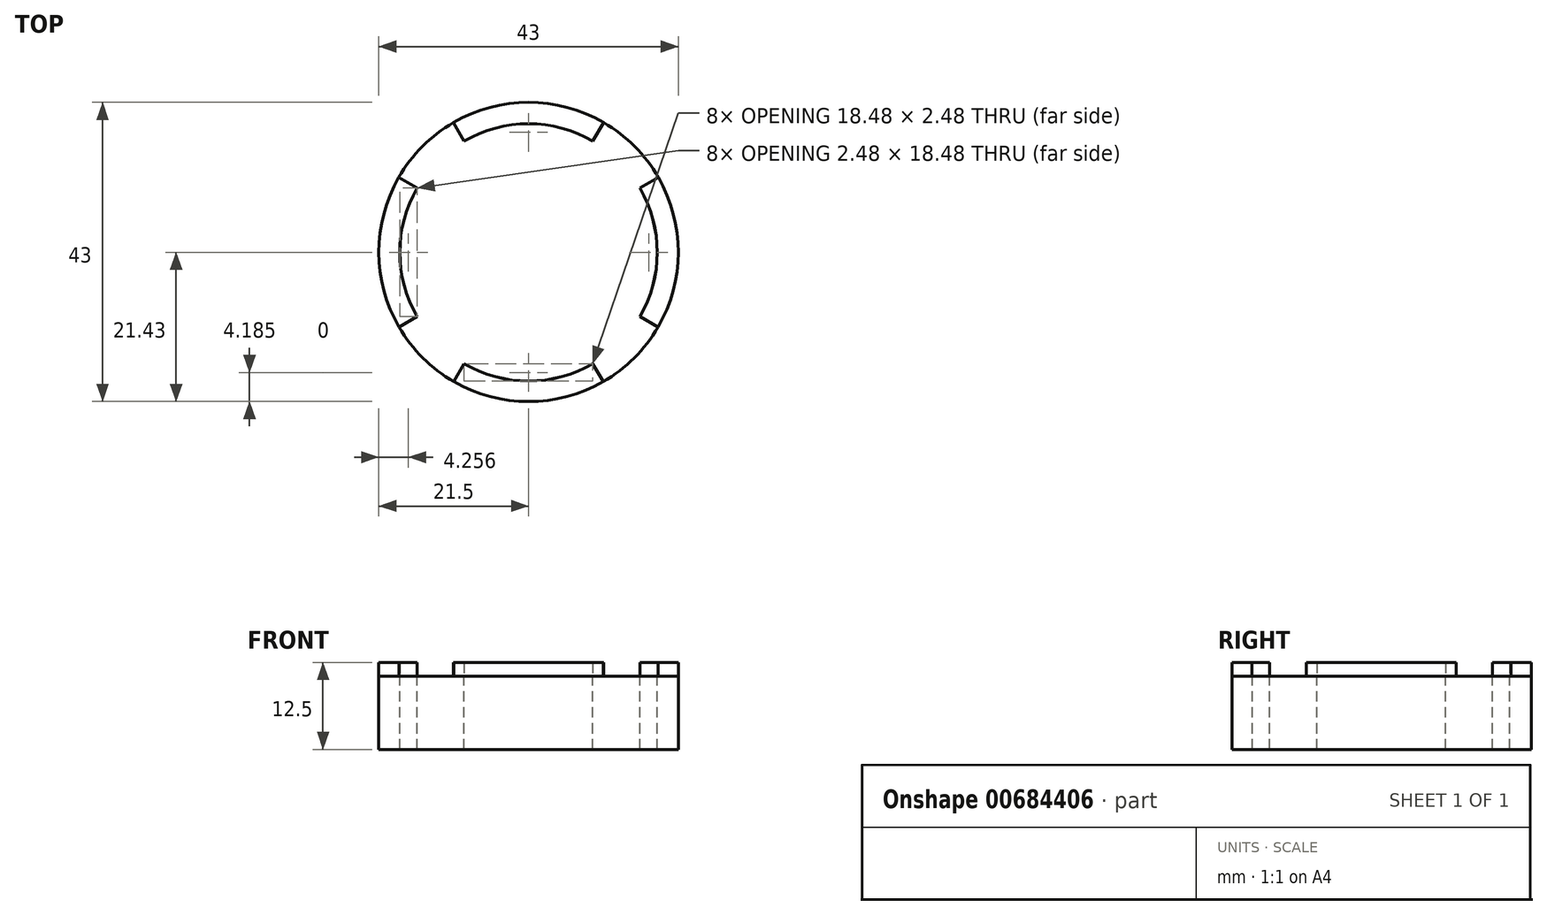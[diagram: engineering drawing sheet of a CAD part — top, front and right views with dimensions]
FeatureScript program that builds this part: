
annotation { "Feature Type Name" : "Feature", "Feature Type Description" : "" }
export const myFeature = defineFeature(function(context is Context, id is Id, definition is map)
    precondition{}
    {
        {
            var Q0;
            Q0=qCreatedBy(makeId("Top.planeOp"),FACE);
            var sketch = newSketch(context, id + "F0", { "sketchPlane" : qUnion([Q0])});
            skCircle(sketch, "E0", {"center": v(0, 0.07) * mm, "radius": 23.75 * mm, "construction": true});
            skCircle(sketch, "E1", {"center": v(0, 0.07) * mm, "radius": 22.5 * mm, "construction": true});
            skCircle(sketch, "E2", {"center": v(0, 0.07) * mm, "radius": 1.02 * mm, "construction": true});
            skLineSegment(sketch, "E3", {"start": v(-23.75, 0.07) * mm, "end": v(23.75, 0.07) * mm, "construction": true});
            skCircle(sketch, "E4", {"center": v(4, 0.07) * mm, "radius": 1.02 * mm, "construction": true});
            skCircle(sketch, "E5", {"center": v(-4, 0.07) * mm, "radius": 1.02 * mm, "construction": true});
            skCircle(sketch, "E6", {"center": v(0, 4.08) * mm, "radius": 1.02 * mm, "construction": true});
            skCircle(sketch, "E7", {"center": v(0, -3.92) * mm, "radius": 1.02 * mm, "construction": true});
            skCircle(sketch, "E8.1.0.0", {"center": v(12, 4.08) * mm, "radius": 1.02 * mm, "construction": true});
            skCircle(sketch, "E8.1.0.1", {"center": v(16, 0.08) * mm, "radius": 1.02 * mm, "construction": true});
            skCircle(sketch, "E8.1.0.2", {"center": v(12, -3.92) * mm, "radius": 1.02 * mm, "construction": true});
            skCircle(sketch, "E8.1.0.3", {"center": v(8, 0.08) * mm, "radius": 1.02 * mm, "construction": true});
            skCircle(sketch, "E8.1.0.4", {"center": v(12, 0.08) * mm, "radius": 1.02 * mm, "construction": true});
            skCircle(sketch, "E9.1.0.0", {"center": v(-12, 4.08) * mm, "radius": 1.02 * mm, "construction": true});
            skCircle(sketch, "E9.1.0.1", {"center": v(-16, 0.07) * mm, "radius": 1.02 * mm, "construction": true});
            skCircle(sketch, "E9.1.0.2", {"center": v(-12, -3.92) * mm, "radius": 1.02 * mm, "construction": true});
            skCircle(sketch, "E9.1.0.3", {"center": v(-8, 0.07) * mm, "radius": 1.02 * mm, "construction": true});
            skCircle(sketch, "E9.1.0.4", {"center": v(-12, 0.07) * mm, "radius": 1.02 * mm, "construction": true});
            skLineSegment(sketch, "E9.direction1", {"start": v(0, 0.07) * mm, "end": v(-12, 0.07) * mm, "construction": true});
            skLineSegment(sketch, "E10", {"start": v(0, 23.82) * mm, "end": v(0, -23.68) * mm, "construction": true});
            skCircle(sketch, "E11.1.0.0", {"center": v(-16, 12.07) * mm, "radius": 1.02 * mm, "construction": true});
            skCircle(sketch, "E11.1.0.1", {"center": v(-12, 8.08) * mm, "radius": 1.02 * mm, "construction": true});
            skCircle(sketch, "E11.1.0.2", {"center": v(-12, 12.07) * mm, "radius": 1.02 * mm, "construction": true});
            skCircle(sketch, "E11.1.0.3", {"center": v(-8, 12.07) * mm, "radius": 1.02 * mm, "construction": true});
            skCircle(sketch, "E11.1.0.4", {"center": v(-4, 12.07) * mm, "radius": 1.02 * mm, "construction": true});
            skCircle(sketch, "E11.1.0.5", {"center": v(0, 16.08) * mm, "radius": 1.02 * mm, "construction": true});
            skCircle(sketch, "E11.1.0.6", {"center": v(4, 12.07) * mm, "radius": 1.02 * mm, "construction": true});
            skCircle(sketch, "E11.1.0.7", {"center": v(0, 12.07) * mm, "radius": 1.02 * mm, "construction": true});
            skCircle(sketch, "E11.1.0.8", {"center": v(0, 8.08) * mm, "radius": 1.02 * mm, "construction": true});
            skCircle(sketch, "E11.1.0.9", {"center": v(8, 12.08) * mm, "radius": 1.02 * mm, "construction": true});
            skCircle(sketch, "E11.1.0.10", {"center": v(12, 12.08) * mm, "radius": 1.02 * mm, "construction": true});
            skCircle(sketch, "E11.1.0.11", {"center": v(16, 12.08) * mm, "radius": 1.02 * mm, "construction": true});
            skCircle(sketch, "E11.1.0.12", {"center": v(12, 8.08) * mm, "radius": 1.02 * mm, "construction": true});
            skCircle(sketch, "E11.1.0.13", {"center": v(12, 16.08) * mm, "radius": 1.02 * mm, "construction": true});
            skCircle(sketch, "E11.1.0.14", {"center": v(-12, 16.08) * mm, "radius": 1.02 * mm, "construction": true});
            skLineSegment(sketch, "E11.direction1", {"start": v(0, 0.07) * mm, "end": v(0, 12.07) * mm, "construction": true});
            skCircle(sketch, "E12.1.0.0", {"center": v(-16, -11.93) * mm, "radius": 1.02 * mm, "construction": true});
            skCircle(sketch, "E12.1.0.1", {"center": v(-12, -15.92) * mm, "radius": 1.02 * mm, "construction": true});
            skCircle(sketch, "E12.1.0.2", {"center": v(-12, -11.93) * mm, "radius": 1.02 * mm, "construction": true});
            skCircle(sketch, "E12.1.0.3", {"center": v(-12, -7.92) * mm, "radius": 1.02 * mm, "construction": true});
            skCircle(sketch, "E12.1.0.4", {"center": v(-8, -11.93) * mm, "radius": 1.02 * mm, "construction": true});
            skCircle(sketch, "E12.1.0.5", {"center": v(-4, -11.93) * mm, "radius": 1.02 * mm, "construction": true});
            skCircle(sketch, "E12.1.0.6", {"center": v(0, -7.92) * mm, "radius": 1.02 * mm, "construction": true});
            skCircle(sketch, "E12.1.0.7", {"center": v(0, -11.93) * mm, "radius": 1.02 * mm, "construction": true});
            skCircle(sketch, "E12.1.0.8", {"center": v(0, -15.92) * mm, "radius": 1.02 * mm, "construction": true});
            skCircle(sketch, "E12.1.0.9", {"center": v(4, -11.93) * mm, "radius": 1.02 * mm, "construction": true});
            skCircle(sketch, "E12.1.0.10", {"center": v(8, -11.92) * mm, "radius": 1.02 * mm, "construction": true});
            skCircle(sketch, "E12.1.0.11", {"center": v(12, -11.92) * mm, "radius": 1.02 * mm, "construction": true});
            skCircle(sketch, "E12.1.0.12", {"center": v(16, -11.92) * mm, "radius": 1.02 * mm, "construction": true});
            skCircle(sketch, "E12.1.0.13", {"center": v(12, -7.92) * mm, "radius": 1.02 * mm, "construction": true});
            skCircle(sketch, "E12.1.0.14", {"center": v(12, -15.92) * mm, "radius": 1.02 * mm, "construction": true});
            skLineSegment(sketch, "E12.direction1", {"start": v(0, 0.07) * mm, "end": v(0, -11.93) * mm, "construction": true});
            skCircle(sketch, "E13", {"center": v(0, 0) * mm, "radius": 18.48 * mm});
            skLineSegment(sketch, "E14", {"start": v(0, 0) * mm, "end": v(-9.24, 16) * mm, "construction": true});
            skCircle(sketch, "E15", {"center": v(0, 0.07) * mm, "radius": 21.5 * mm});
            skLineSegment(sketch, "E16", {"start": v(-9.24, 16) * mm, "end": v(-10.78, 18.67) * mm});
            skLineSegment(sketch, "E17", {"start": v(0, 0) * mm, "end": v(9.24, 16) * mm, "construction": true});
            skLineSegment(sketch, "E18", {"start": v(9.24, 16) * mm, "end": v(10.78, 18.67) * mm});
            skArc(sketch, "E19", {"start": v(9.24, 16) * mm, "mid": v(0, 18.48) * mm, "end": v(-9.24, 16) * mm});
            skLineSegment(sketch, "E20.1.0", {"start": v(-16, 9.24) * mm, "end": v(-18.67, 10.78) * mm});
            skLineSegment(sketch, "E20.2.0", {"start": v(-9.24, -16) * mm, "end": v(-10.78, -18.67) * mm});
            skLineSegment(sketch, "E20.3.0", {"start": v(16, -9.24) * mm, "end": v(18.67, -10.78) * mm});
            skLineSegment(sketch, "E21.1.0", {"start": v(-16, -9.24) * mm, "end": v(-18.67, -10.78) * mm});
            skLineSegment(sketch, "E21.2.0", {"start": v(9.24, -16) * mm, "end": v(10.78, -18.67) * mm});
            skLineSegment(sketch, "E22.1.3.0", {"start": v(16, 9.24) * mm, "end": v(18.67, 10.78) * mm});
            skArc(sketch, "E23", {"start": v(-16, 9.24) * mm, "mid": v(-18.48, 0) * mm, "end": v(-16, -9.24) * mm});
            skArc(sketch, "E24", {"start": v(-9.24, -16) * mm, "mid": v(0, -18.48) * mm, "end": v(9.24, -16) * mm});
            skArc(sketch, "E25", {"start": v(16, -9.24) * mm, "mid": v(18.48, 0) * mm, "end": v(16, 9.24) * mm});
            skSolve(sketch);
        }
        {
            var Q0;
            {var subQ1=sQuery(id+"F0.wireOp",EDGE,"E16");Q0=makeQuery(id+"F0.imprint","IMPRINT",FACE,{"disambiguationData":[TD([[makeQuery(id+"F0.imprint","IMPRINT",EDGE,{"derivedFrom":subQ1}),-1.0]])]});}
            var Q1;
            {var subQ4=sQuery(id+"F0.wireOp",EDGE,"E22.1.3.0");var subQ6=sQuery(id+"F0.wireOp",EDGE,"E15");var subQ7=makeQuery(id+"F0.imprint","INTERSECT",VERTEX,{"derivedFrom":[subQ6,subQ4]});Q1=makeQuery(id+"F0.imprint","IMPRINT",FACE,{"disambiguationData":[TD([[makeQuery(id+"F0.imprint","IMPRINT",EDGE,{"disambiguationData":[TD([[subQ7,1.0]])],"derivedFrom":subQ6}),1.0]])]});}
            var Q2;
            {var subQ5=sQuery(id+"F0.wireOp",EDGE,"E24");Q2=makeQuery(id+"F0.imprint","IMPRINT",FACE,{"disambiguationData":[TD([[makeQuery(id+"F0.imprint","IMPRINT",EDGE,{"derivedFrom":subQ5}),-1.0]])]});}
            var Q3;
            {var subQ1=sQuery(id+"F0.wireOp",EDGE,"E20.1.0");var subQ6=sQuery(id+"F0.wireOp",EDGE,"E15");var subQ7=makeQuery(id+"F0.imprint","INTERSECT",VERTEX,{"derivedFrom":[subQ6,subQ1]});Q3=makeQuery(id+"F0.imprint","IMPRINT",FACE,{"disambiguationData":[TD([[makeQuery(id+"F0.imprint","IMPRINT",EDGE,{"disambiguationData":[TD([[subQ7,-1.0]])],"derivedFrom":subQ6}),1.0]])]});}
            extrude(context, id + "F1", {"entities" : qUnion([Q0, Q1, Q2, Q3]), "depth" : 2 * mm, "offsetDistance" : 25 * mm});
        }
        {
            var Q0;
            {var subQ4=sQuery(id+"F0.wireOp",EDGE,"E19");Q0=makeQuery(id+"F0.imprint","IMPRINT",FACE,{"disambiguationData":[TD([[makeQuery(id+"F0.imprint","IMPRINT",EDGE,{"derivedFrom":subQ4}),1.0]])]});}
            var Q1;
            {var subQ0=sQuery(id+"F0.wireOp",EDGE,"E16");Q1=makeQuery(id+"F0.imprint","IMPRINT",FACE,{"disambiguationData":[TD([[makeQuery(id+"F0.imprint","IMPRINT",EDGE,{"derivedFrom":subQ0}),1.0]])]});}
            var Q2;
            {var subQ1=sQuery(id+"F0.wireOp",EDGE,"E16");Q2=makeQuery(id+"F0.imprint","IMPRINT",FACE,{"disambiguationData":[TD([[makeQuery(id+"F0.imprint","IMPRINT",EDGE,{"derivedFrom":subQ1}),-1.0]])]});}
            var Q3;
            {var subQ0=sQuery(id+"F0.wireOp",EDGE,"E18");Q3=makeQuery(id+"F0.imprint","IMPRINT",FACE,{"disambiguationData":[TD([[makeQuery(id+"F0.imprint","IMPRINT",EDGE,{"derivedFrom":subQ0}),-1.0]])]});}
            var Q4;
            {var subQ4=sQuery(id+"F0.wireOp",EDGE,"E22.1.3.0");var subQ6=sQuery(id+"F0.wireOp",EDGE,"E15");var subQ7=makeQuery(id+"F0.imprint","INTERSECT",VERTEX,{"derivedFrom":[subQ6,subQ4]});Q4=makeQuery(id+"F0.imprint","IMPRINT",FACE,{"disambiguationData":[TD([[makeQuery(id+"F0.imprint","IMPRINT",EDGE,{"disambiguationData":[TD([[subQ7,1.0]])],"derivedFrom":subQ6}),1.0]])]});}
            var Q5;
            {var subQ3=sQuery(id+"F0.wireOp",EDGE,"E21.2.0");var subQ5=sQuery(id+"F0.wireOp",EDGE,"E15");var subQ7=makeQuery(id+"F0.imprint","INTERSECT",VERTEX,{"derivedFrom":[subQ5,subQ3]});Q5=makeQuery(id+"F0.imprint","IMPRINT",FACE,{"disambiguationData":[TD([[makeQuery(id+"F0.imprint","IMPRINT",EDGE,{"disambiguationData":[TD([[subQ7,-1.0]])],"derivedFrom":subQ5}),1.0]])]});}
            var Q6;
            {var subQ5=sQuery(id+"F0.wireOp",EDGE,"E24");Q6=makeQuery(id+"F0.imprint","IMPRINT",FACE,{"disambiguationData":[TD([[makeQuery(id+"F0.imprint","IMPRINT",EDGE,{"derivedFrom":subQ5}),-1.0]])]});}
            var Q7;
            {var subQ3=sQuery(id+"F0.wireOp",EDGE,"E21.1.0");var subQ5=sQuery(id+"F0.wireOp",EDGE,"E15");var subQ6=makeQuery(id+"F0.imprint","INTERSECT",VERTEX,{"derivedFrom":[subQ5,subQ3]});Q7=makeQuery(id+"F0.imprint","IMPRINT",FACE,{"disambiguationData":[TD([[makeQuery(id+"F0.imprint","IMPRINT",EDGE,{"disambiguationData":[TD([[subQ6,-1.0]])],"derivedFrom":subQ5}),1.0]])]});}
            var Q8;
            {var subQ1=sQuery(id+"F0.wireOp",EDGE,"E20.1.0");var subQ6=sQuery(id+"F0.wireOp",EDGE,"E15");var subQ7=makeQuery(id+"F0.imprint","INTERSECT",VERTEX,{"derivedFrom":[subQ6,subQ1]});Q8=makeQuery(id+"F0.imprint","IMPRINT",FACE,{"disambiguationData":[TD([[makeQuery(id+"F0.imprint","IMPRINT",EDGE,{"disambiguationData":[TD([[subQ7,-1.0]])],"derivedFrom":subQ6}),1.0]])]});}
            extrude(context, id + "F2", {"entities" : qUnion([Q0, Q1, Q2, Q3, Q4, Q5, Q6, Q7, Q8]), "oppositeDirection" : true, "depth" : 10.5 * mm, "offsetDistance" : 25 * mm});
        }
    });
